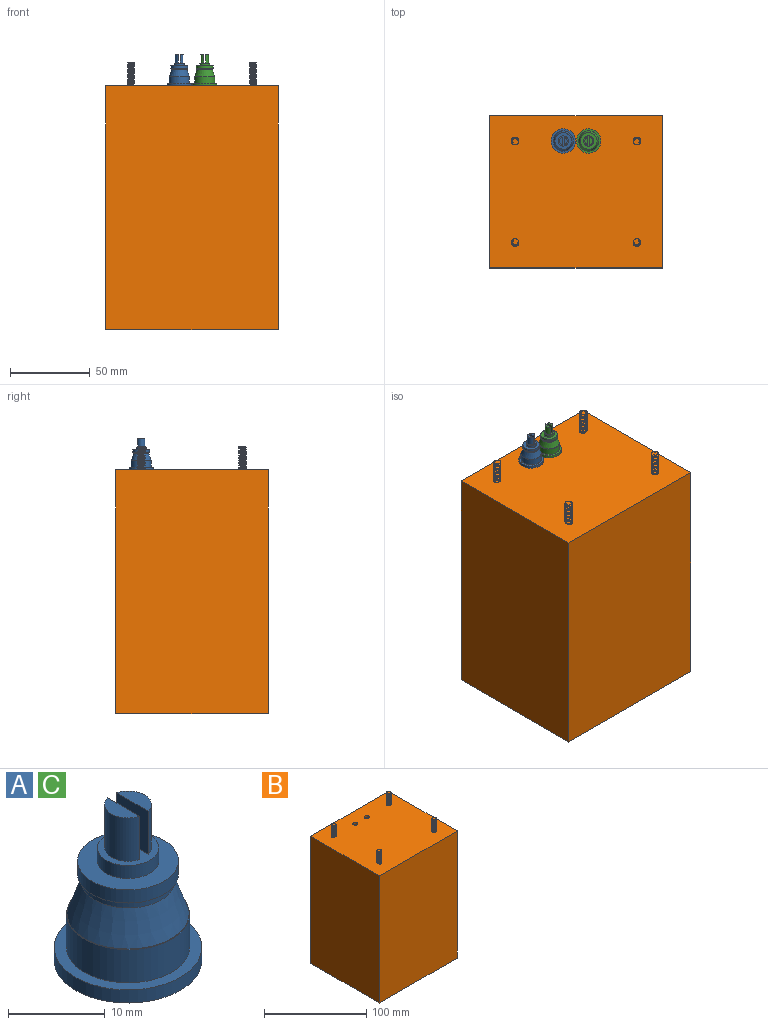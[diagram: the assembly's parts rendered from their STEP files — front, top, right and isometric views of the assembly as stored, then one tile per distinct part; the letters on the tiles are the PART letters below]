
ASSEMBLY  parts=3 mates=2
PART A: 19 faces, bbox 15.2x15.2x19.7 mm
  f0: cylinder r=2.41mm len=5.46mm, axis (0,0,1), area 34.4mm2, adj f1,f14,f17
  f1: plane 4.66x1.78mm, normal (0,0,1), area 6.1mm2, adj f0,f17
  f2: plane 15.24x15.24mm, normal (0,0,-1), area 182.4mm2, adj f3
  f3: cylinder r=7.62mm len=15.24mm, axis (0,0,1), area 79mm2, adj f2,f4
  f4: plane 15.24x15.24mm, normal (0,0,1), area 55.7mm2, adj f3,f5
  f5: cylinder r=6.35mm len=12.7mm, axis (0,0,1), area 167.2mm2, adj f4,f6
  f6: plane 12.7x12.7mm, normal (0,0,1), area 2.4mm2, adj f5,f7
  f7: torus R=6.29mm, axis (0,0,1), area 1.2mm2, adj f6,f8
  f8: cone r=6.27mm half-angle=19deg, axis (0,0,-1), area 153.9mm2, adj f7,f9
  f9: cylinder r=4.83mm len=9.65mm, axis (0,0,1), area 27mm2, adj f8,f10
  f10: plane 10.41x10.41mm, normal (0,0,-1), area 12mm2, adj f9,f11
  f11: cylinder r=5.21mm len=10.41mm, axis (0,0,1), area 54mm2, adj f10,f12
  f12: plane 10.41x10.41mm, normal (0,0,1), area 53.5mm2, adj f11,f13
  f13: cylinder r=3.17mm len=6.35mm, axis (0,0,1), area 32.9mm2, adj f12,f14
  f14: plane 6.35x6.35mm, normal (0,0,1), area 19.4mm2, adj f0,f13,f15,f17,f18
  f15: cylinder r=2.41mm len=5.46mm, axis (0,0,1), area 34.4mm2, adj f14,f16,f18
  f16: plane 4.66x1.78mm, normal (0,0,1), area 6.1mm2, adj f15,f18
  f17: plane 5.46x4.66mm, normal (1,0,0), area 25.4mm2, adj f0,f1,f14
  f18: plane 5.46x4.66mm, normal (-1,0,0), area 25.4mm2, adj f14,f15,f16
PART B: 34 faces, bbox 108.6x95.9x168.2 mm
  f0: plane 108.62x95.92mm, normal (0,0,1), area 10180.2mm2, adj f1,f3,f4,f5,f7,f9,f10,f11
  f1: cylinder r=2.41mm len=14.61mm, axis (0,0,-1), area -4.4mm2, adj f0,f2,f3,f4,f5,f6
  f2: plane 4.83x4.41mm, normal (0,0,1), area 15.3mm2, adj f1,f5,f6
  f3: plane 0.86x0.52mm, normal (0.95,-0.31,0), area 0.2mm2, adj f0,f1,f5
  f4: bspline ~15.16x5.57mm, area 172.3mm2, adj f0,f1,f5,f6
  f5: bspline ~15.16x5.57mm, area 173.6mm2, adj f0,f1,f2,f3,f4
  f6: plane 0.9x0.52mm, normal (0,1,0), area 0.2mm2, adj f1,f2,f4
  f7: cylinder r=2.41mm len=14.61mm, axis (0,0,-1), area 14mm2, adj f0,f8,f9,f10,f11,f12
  f8: plane 4.83x4.41mm, normal (0,0,1), area 15.3mm2, adj f7,f11,f12
  f9: plane 0.86x0.52mm, normal (-0.95,-0.31,0), area 0.2mm2, adj f0,f7,f11
  f10: bspline ~15.16x5.57mm, area 172.3mm2, adj f0,f7,f11,f12
  f11: bspline ~15.16x5.57mm, area 173.6mm2, adj f0,f7,f8,f9,f10
  f12: plane 0.9x0.52mm, normal (0,1,0), area 0.2mm2, adj f7,f8,f10
  f13: cylinder r=2.41mm len=14.61mm, axis (0,0,-1), area 14mm2, adj f0,f14,f15,f16,f17,f18
  f14: plane 4.83x4.41mm, normal (0,0,1), area 15.3mm2, adj f13,f17,f18
  f15: plane 0.86x0.52mm, normal (0.95,0.31,0), area 0.2mm2, adj f0,f13,f17
  f16: bspline ~15.16x5.57mm, area 172.3mm2, adj f0,f13,f17,f18
  f17: bspline ~15.16x5.57mm, area 173.6mm2, adj f0,f13,f14,f15,f16
  f18: plane 0.9x0.52mm, normal (0,-1,0), area 0.2mm2, adj f13,f14,f16
  f19: cylinder r=2.41mm len=14.61mm, axis (0,0,-1), area -4.4mm2, adj f0,f20,f21,f22,f23,f24
  f20: plane 4.83x4.41mm, normal (0,0,1), area 15.3mm2, adj f19,f23,f24
  f21: plane 0.86x0.52mm, normal (-0.95,0.31,0), area 0.2mm2, adj f0,f19,f23
  f22: bspline ~15.16x5.57mm, area 172.3mm2, adj f0,f19,f23,f24
  f23: bspline ~15.16x5.57mm, area 173.6mm2, adj f0,f19,f20,f21,f22
  f24: plane 0.9x0.52mm, normal (0,-1,0), area 0.2mm2, adj f19,f20,f22
  f25: plane 152.4x95.25mm, normal (1,0,0), area 14516.1mm2, adj f0,f26,f28,f29
  f26: plane 152.4x107.95mm, normal (0,1,0), area 16451.6mm2, adj f0,f25,f27,f29
  f27: plane 152.4x95.25mm, normal (-1,0,0), area 14516.1mm2, adj f0,f26,f28,f29
  f28: plane 152.4x107.95mm, normal (0,-1,0), area 16451.6mm2, adj f0,f25,f27,f29
  f29: plane 107.95x95.25mm, normal (0,0,-1), area 10282.2mm2, adj f25,f26,f27,f28
  f30: cylinder r=2.54mm len=5.08mm, axis (0,0,1), area 40.5mm2, adj f0,f31
  f31: plane 5.08x5.08mm, normal (0,0,1), area 20.3mm2, adj f30
  f32: cylinder r=2.54mm len=5.08mm, axis (0,0,1), area 40.5mm2, adj f0,f33
  f33: plane 5.08x5.08mm, normal (0,0,1), area 20.3mm2, adj f32
PART C: same geometry as A
PLACE A t=(-3.86,-2.52,13.96)mm
PLACE B t=(4.07,-34.27,13.96)mm
PLACE C t=(12.01,-2.52,13.96)mm
MATE fastened C.f0 <-> B.f32  axis (0,0,-1) through (12.01,-2.52,13.96)mm
MATE fastened A.f0 <-> B.f30  axis (0,0,-1) through (-3.86,-2.52,13.96)mm
